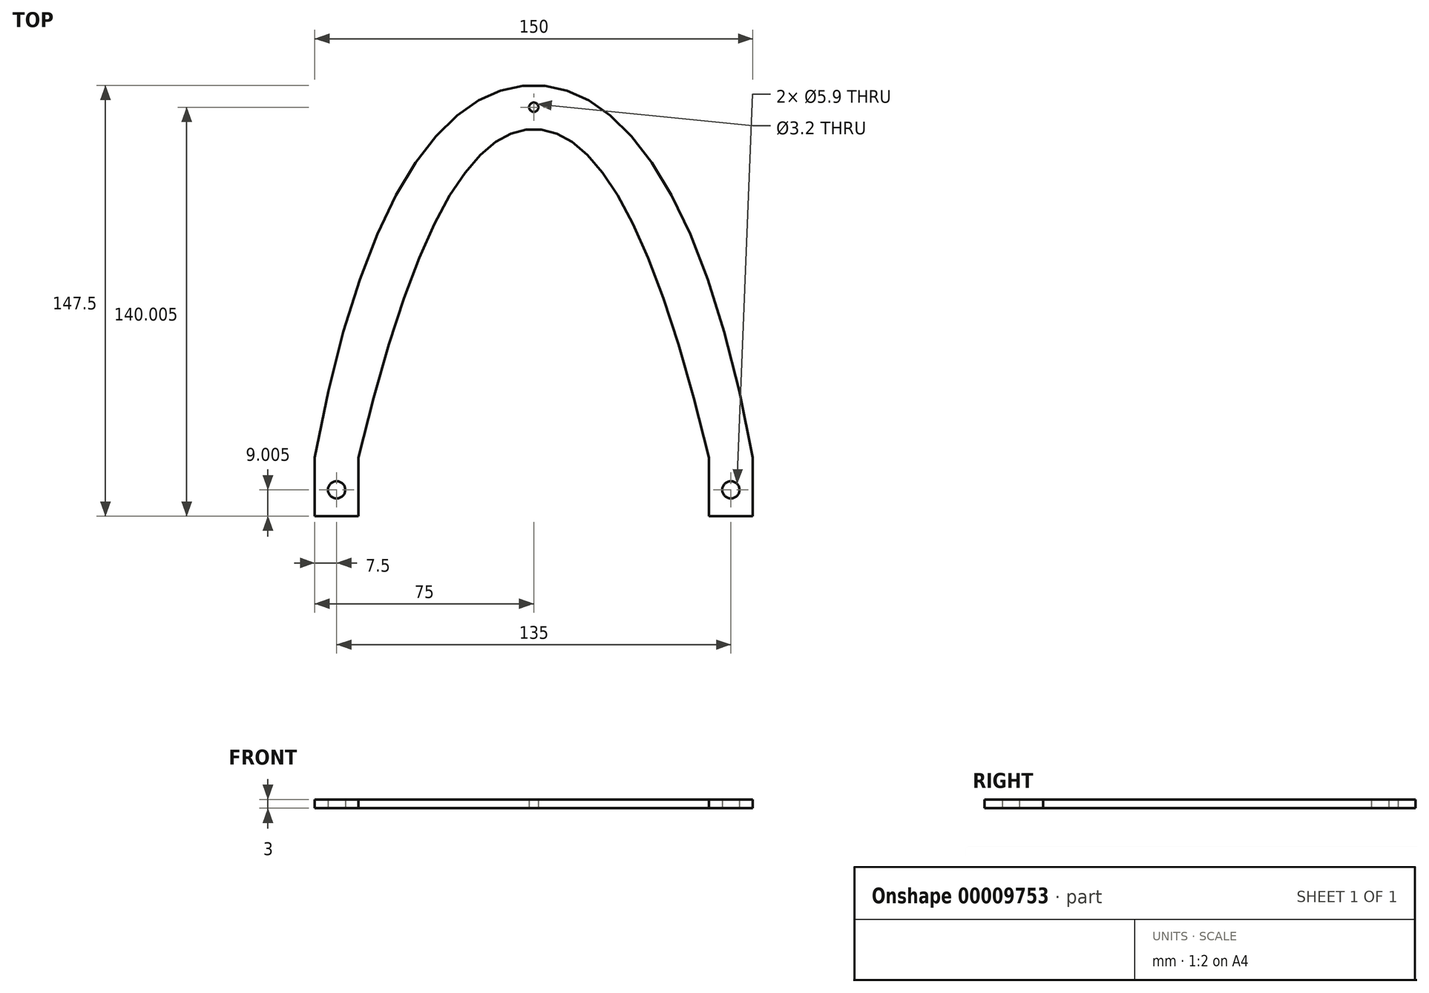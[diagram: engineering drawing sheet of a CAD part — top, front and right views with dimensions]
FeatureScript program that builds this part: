
annotation { "Feature Type Name" : "Feature", "Feature Type Description" : "" }
export const myFeature = defineFeature(function(context is Context, id is Id, definition is map)
    precondition{}
    {
        {
            var Q0;
            Q0=qCreatedBy(makeId("Top.planeOp"),FACE);
            var sketch = newSketch(context, id + "F0", { "sketchPlane" : qUnion([Q0])});
            skLineSegment(sketch, "E0.rect.bottom", {"start": v(75, -99.32) * mm, "end": v(60, -99.32) * mm});
            skLineSegment(sketch, "E0.rect.left", {"start": v(75, -99.32) * mm, "end": v(75, -79.32) * mm});
            skLineSegment(sketch, "E0.rect.right", {"start": v(-75, -99.32) * mm, "end": v(-75, -79.32) * mm});
            skPoint(sketch, "E0.rect.middle", {"position": v(0, 0) * mm});
            skLineSegment(sketch, "E1", {"start": v(-60, -99.32) * mm, "end": v(-75, -99.32) * mm});
            skLineSegment(sketch, "E2", {"start": v(60, -79.32) * mm, "end": v(60, -99.32) * mm});
            skLineSegment(sketch, "E3", {"start": v(-60, -79.32) * mm, "end": v(-60, -79.32) * mm});
            skLineSegment(sketch, "E4", {"start": v(-75, -79.32) * mm, "end": v(-75, -79.32) * mm});
            skLineSegment(sketch, "E5", {"start": v(75, -79.32) * mm, "end": v(75, -79.32) * mm});
            skLineSegment(sketch, "E6", {"start": v(-60, -99.32) * mm, "end": v(-60, -79.32) * mm});
            skLineSegment(sketch, "E7", {"start": v(60, -79.32) * mm, "end": v(60, -79.32) * mm});
            skFitSpline(sketch, "E8", {"points": [v(-60, -79.32) * mm, v(0, 33.18) * mm, v(60, -79.32) * mm], "startDerivative": vector(119.53, 500.98) * mm, "endDerivative": vector(119.53, -500.98) * mm});
            skFitSpline(sketch, "E9", {"points": [v(-75, -79.32) * mm, v(0, 48.18) * mm, v(75, -79.32) * mm], "startDerivative": vector(100.37, 554.5) * mm, "endDerivative": vector(100.37, -554.5) * mm});
            skCircle(sketch, "E10", {"center": v(67.5, -90.32) * mm, "radius": 2.95 * mm});
            skCircle(sketch, "E11", {"center": v(-67.5, -90.32) * mm, "radius": 2.95 * mm});
            skCircle(sketch, "E12", {"center": v(0, 40.68) * mm, "radius": 1.6 * mm});
            skLineSegment(sketch, "E13", {"start": v(-60, -99.32) * mm, "end": v(60, -99.32) * mm, "construction": true});
            skLineSegment(sketch, "E14", {"start": v(67.5, -90.32) * mm, "end": v(67.5, -99.32) * mm, "construction": true});
            skLineSegment(sketch, "E15", {"start": v(-67.5, -90.32) * mm, "end": v(-67.5, -99.32) * mm, "construction": true});
            skSolve(sketch);
        }
        {
            var Q0;
            Q0=makeQuery(id+"F0.imprint","IMPRINT",FACE,{"disambiguationData":[TD([[makeQuery(id+"F0.imprint","IMPRINT",EDGE,{"derivedFrom":sQuery(id+"F0.wireOp",EDGE,"E0.rect.bottom")}),-1.0]])]});
            extrude(context, id + "F1", {"entities" : qUnion([Q0]), "depth" : 3 * mm});
        }
    });
